# Revit family: Haworth_Belong_Screen
name_source: partatom
category: Furniture Systems
revit_build: Autodesk Revit 2018 (Build: 20170223_1515(x64)
units: mm (PartAtom-declared; Revit-internal decimal feet)

## family parameters
Always vertical = Yes
Cut with Voids When Loaded = No
OmniClass Number = 23.40.70.14.64.21
OmniClass Title = Systems Furniture
Part Type = Normal
Room Calculation Point = No
Round Connector Dimension = Use Diameter
Shared = No
Work Plane-Based = No

## types (4) — shared parameters
Assembly Code = E2020200
Bracket Finish = Haworth _ Metal _ Brushed Aluminum
Bracket Offset = 3"
Custom Size = No
Description = Haworth_Belong-Screen
Manufacturer = Haworth
Min. Width = 24"
Model = Haworth - Belong - Screen
Revision Number = 3
Screen Finish = Haworth _ Glass _ Clear
Size = Verify Final Dim. w/ Haworth
Sustainability Info = https://www.haworth.com
URL = www.haworth.com
URL - Product = http://www.haworth.com
Warranty = http://www.haworth.com
Worksurface Thickness = 1 3/16"

## per-type parameters (varying)
| type | Actual Height | Actual Mounting Height | Actual Width | Bracket Spacing | Height | Max. Height | Max. Width | Middle Bracket | Min. Height | Panel Bottom Offset | Screen Depth | Standard Heights | Standard Widths | Width | Worksurface Height |
| Back or End Screen | 27" | 27 13/16" | 60" | 50" | 27" | 27" | 60" | No | 19" | 0" | 1/2" | 19 or 27 in. | 24-60 in. @ 6 in. increments | 60" | 29" |
| Center Screen | 14" | 27 13/16" | 60" | 50" | 14" | 14" | 96" | Yes | 14" | 1/4" | 1/2" | 14 in. | 24-96 in. @ 6 in. Increments | 60" | 29" |
| Territory Screen | 12" | 29" | 24" | 14" | 12" | 12" | 24" | No | 12" | 1/4" | 1/2" | 12 in. | 24 in. | 24" | 29" |
| Full Modesty or Structural L Screen | 42" | 28 13/16" | 48" | 38" | 42" | 50" | 48" | No | 42" | 0" | 1 1/2" | 42 or 50 in. | 24-48 in. @ 6 in. increments | 48" | 30" |

type visibility flags: 4 boolean params named "<type name>" — each type sets only its own to Yes (folded from table)

## geometry (parser evidence)
native form markers: Sweep x2
no freeform markers — native parametric forms only
